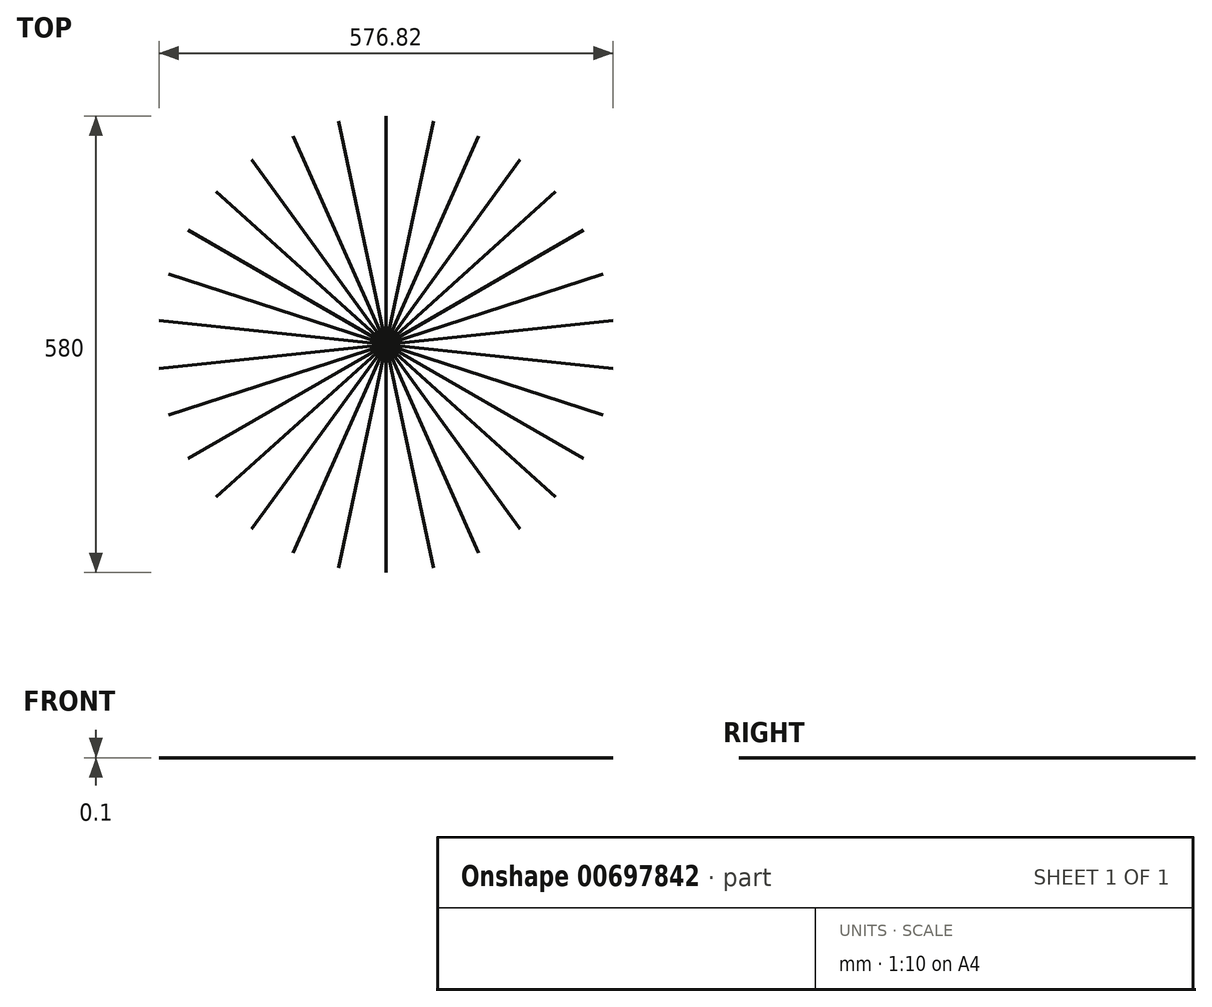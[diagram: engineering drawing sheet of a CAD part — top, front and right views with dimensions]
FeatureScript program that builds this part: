
annotation { "Feature Type Name" : "Feature", "Feature Type Description" : "" }
export const myFeature = defineFeature(function(context is Context, id is Id, definition is map)
    precondition{}
    {
        {
            var Q0;
            Q0=qCreatedBy(makeId("Top.planeOp"),FACE);
            var sketch = newSketch(context, id + "F0", { "sketchPlane" : qUnion([Q0])});
            skLineSegment(sketch, "E0.bottom", {"start": v(0, 0) * mm, "end": v(0.1, 0) * mm});
            skLineSegment(sketch, "E0.top", {"start": v(0, 290) * mm, "end": v(0.1, 290) * mm});
            skLineSegment(sketch, "E0.left", {"start": v(0, 0) * mm, "end": v(0, 290) * mm});
            skLineSegment(sketch, "E0.right", {"start": v(0.1, 0) * mm, "end": v(0.1, 290) * mm});
            skSolve(sketch);
        }
        {
            var Q0;
            Q0=sQuery(id+"F0.wireOp",EDGE,"E0.left");
            extrude(context, id + "F1", {"bodyType" : ToolBodyType.SURFACE, "surfaceEntities" : qUnion([Q0]), "depth" : 0.1 * mm, "offsetDistance" : 25 * mm});
        }
        {
            var Q0;
            Q0=qCreatedBy(makeId("Right.planeOp"),FACE);
            var sketch = newSketch(context, id + "F2", { "sketchPlane" : qUnion([Q0])});
            skLineSegment(sketch, "E1", {"start": v(0, 0) * mm, "end": v(0, 41.99) * mm});
            skSolve(sketch);
        }
        {
            var Q0;
            Q0=makeQuery(id+"F1.opExtrude","SWEPT_BODY",BODY,{"disambiguationData":[OSD([sQuery(id+"F0.wireOp",EDGE,"E0.left")])]});
            var Q1;
            Q1=sQuery(id+"F2.wireOp",EDGE,"E1");
            circularPattern(context, id + "F3", {"entities" : qUnion([Q0]), "axis" : qUnion([Q1]), "angle" : 360 * degree, "instanceCount" : 30, "equalSpace" : true});
        }
    });
